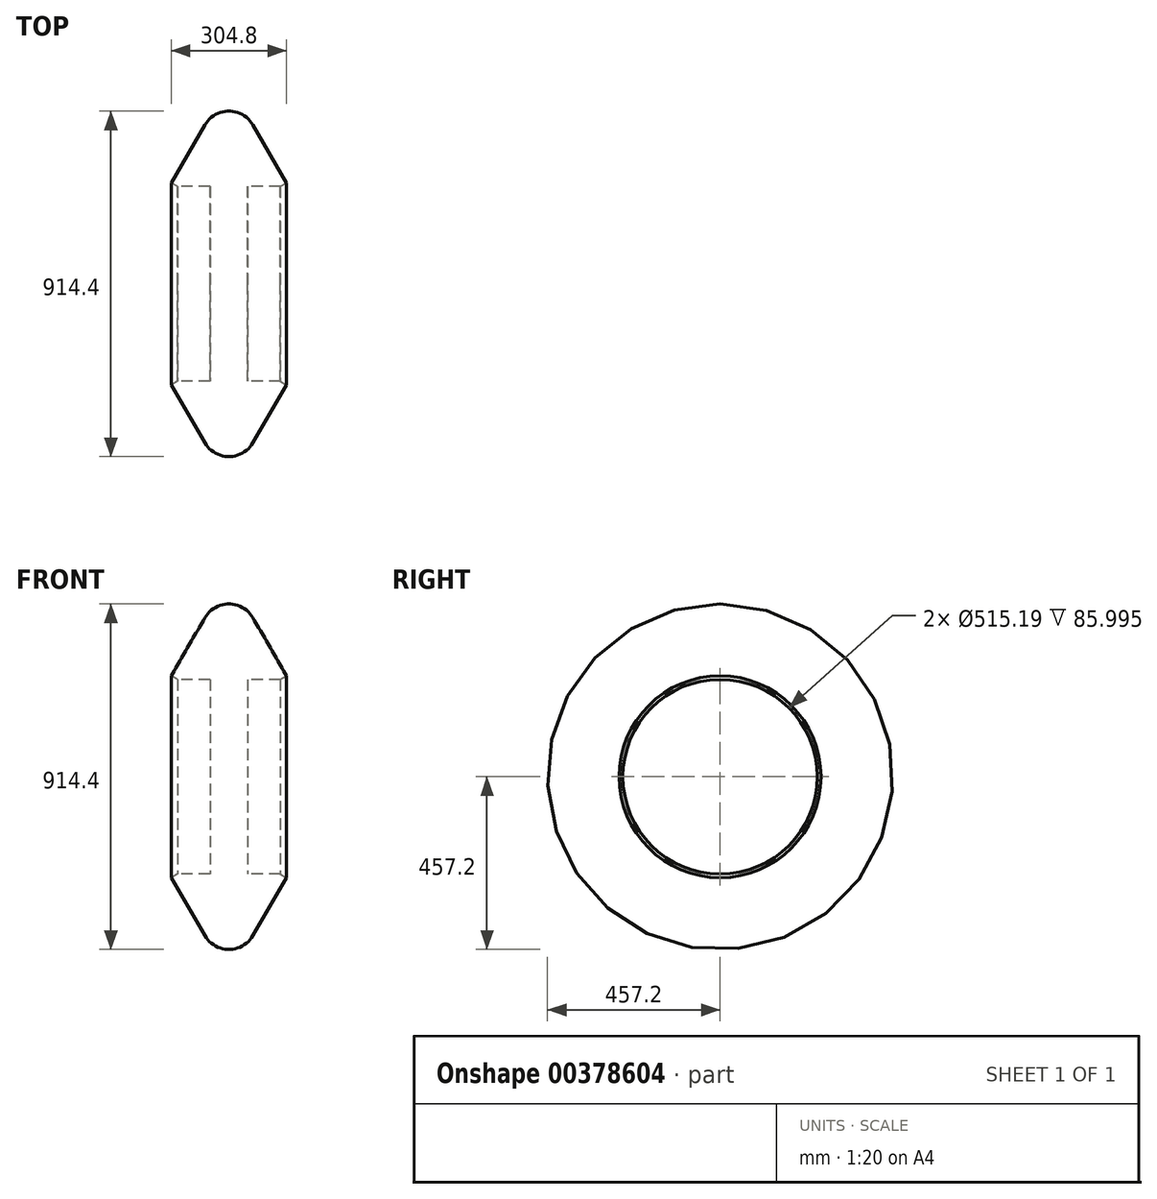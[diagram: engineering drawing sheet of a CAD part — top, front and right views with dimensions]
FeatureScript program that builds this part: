
annotation { "Feature Type Name" : "Feature", "Feature Type Description" : "" }
export const myFeature = defineFeature(function(context is Context, id is Id, definition is map)
    precondition{}
    {
        {
            var Q0;
            Q0=qCreatedBy(makeId("Front.planeOp"),FACE);
            var sketch = newSketch(context, id + "F0", { "sketchPlane" : qUnion([Q0])});
            skLineSegment(sketch, "E0", {"start": v(0, 0) * mm, "end": v(0, 457.2) * mm, "construction": true});
            skLineSegment(sketch, "E1", {"start": v(0, 0) * mm, "end": v(-119.37, 0) * mm, "construction": true});
            skArc(sketch, "E2", {"start": v(0, 0) * mm, "mid": v(36.9, 9.89) * mm, "end": v(63.93, 36.9) * mm});
            skLineSegment(sketch, "E3", {"start": v(63.93, 36.9) * mm, "end": v(152.4, 190.15) * mm});
            skLineSegment(sketch, "E4", {"start": v(152.4, 190.15) * mm, "end": v(136.01, 199.6) * mm});
            skLineSegment(sketch, "E5", {"start": v(136.01, 199.6) * mm, "end": v(50.02, 199.6) * mm});
            skLineSegment(sketch, "E6", {"start": v(50.02, 199.6) * mm, "end": v(50.02, 457.2) * mm});
            skLineSegment(sketch, "E7", {"start": v(0, 457.2) * mm, "end": v(50.02, 457.2) * mm});
            skLineSegment(sketch, "E8.MirrorCS", {"start": v(0, 457.2) * mm, "end": v(-50.02, 457.2) * mm});
            skLineSegment(sketch, "E9.MirrorCS", {"start": v(-50.02, 199.6) * mm, "end": v(-50.02, 457.2) * mm});
            skLineSegment(sketch, "E10.MirrorCS", {"start": v(-136.01, 199.6) * mm, "end": v(-50.02, 199.6) * mm});
            skLineSegment(sketch, "E11.MirrorCS", {"start": v(-152.4, 190.15) * mm, "end": v(-136.01, 199.6) * mm});
            skLineSegment(sketch, "E12.MirrorCS", {"start": v(-63.93, 36.9) * mm, "end": v(-152.4, 190.15) * mm});
            skArc(sketch, "E13.MirrorCS", {"start": v(0, 0) * mm, "mid": v(-36.9, 9.89) * mm, "end": v(-63.93, 36.9) * mm});
            skSolve(sketch);
        }
        {
            var Q0;
            Q0 = qSketchRegion(id + "F0", true);
            var Q1;
            Q1=sQuery(id+"F0.wireOp",EDGE,"E7");
            revolve(context, id + "F1", {"entities" : qUnion([Q0]), "axis" : qUnion([Q1]), "revolveType" : RevolveType.FULL});
        }
    });
